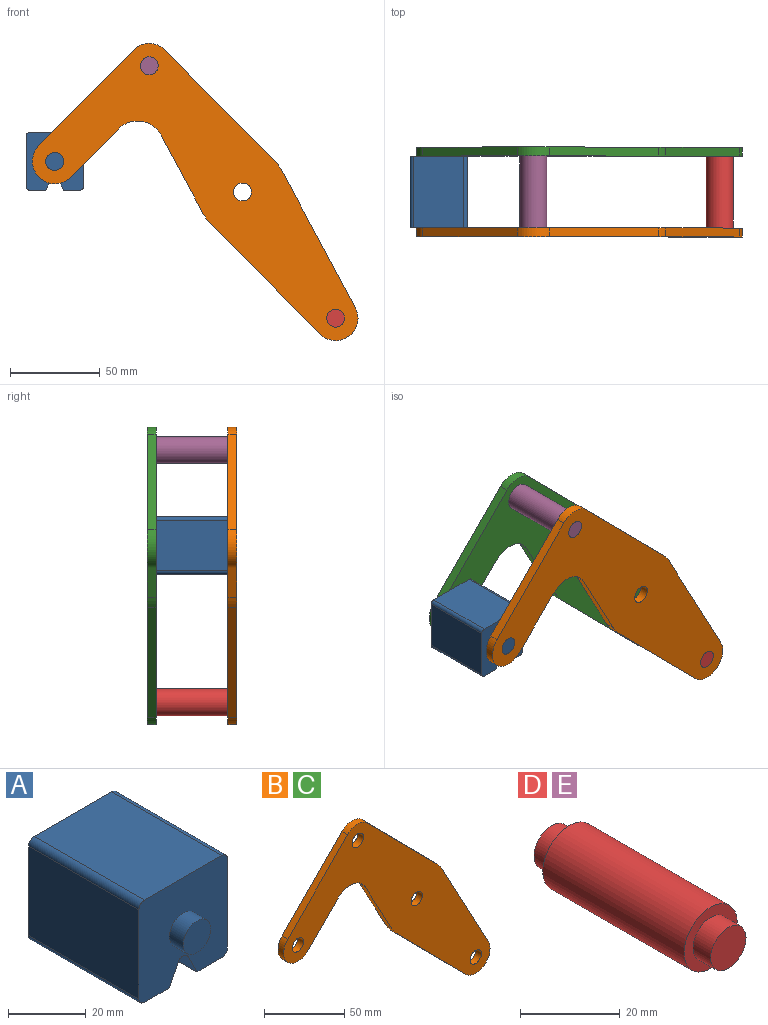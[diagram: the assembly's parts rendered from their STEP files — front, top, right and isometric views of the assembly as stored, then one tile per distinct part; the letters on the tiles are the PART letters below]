
ASSEMBLY  parts=5 mates=3
PART A: 18 faces, bbox 32.1x50x32.1 mm
  f0: plane 40x28.08mm, normal (1,0,0), area 1123.1mm2, adj f4,f10,f13,f14
  f1: plane 40x9.04mm, normal (0,0,-1), area 361.6mm2, adj f2,f4,f10,f14
  f2: plane 40x6.42mm, normal (-0.89,0,-0.45), area 287.2mm2, adj f1,f4,f10,f15
  f3: plane 40x6.42mm, normal (0.89,0,-0.45), area 287.2mm2, adj f4,f5,f10,f15
  f4: plane 32.08x32.08mm, normal (0,-1,0), area 900.6mm2, adj f0,f1,f2,f3,f5,f6,f7,f9
  f5: plane 40x9.04mm, normal (0,0,-1), area 361.6mm2, adj f3,f4,f10,f16
  f6: plane 40x28.08mm, normal (0,0,1), area 1123.1mm2, adj f4,f10,f13,f17
  f7: plane 40x28.08mm, normal (-1,0,0), area 1123.1mm2, adj f4,f10,f16,f17
  f8: plane 10x10mm, normal (0,-1,0), area 78.5mm2, adj f9
  f9: cylinder r=5mm len=10mm, axis (0,1,0), area 157.1mm2, adj f4,f8
  f10: plane 32.08x32.08mm, normal (0,1,0), area 900.6mm2, adj f0,f1,f2,f3,f5,f6,f7,f12
  f11: plane 10x10mm, normal (0,1,0), area 78.5mm2, adj f12
  f12: cylinder r=5mm len=10mm, axis (0,-1,0), area 157.1mm2, adj f10,f11
  f13: cylinder r=2mm len=40mm, axis (0,1,0), area 125.7mm2, adj f0,f4,f6,f10
  f14: cylinder r=2mm len=40mm, axis (0,-1,0), area 125.7mm2, adj f0,f1,f4,f10
  f15: cylinder r=2mm len=40mm, axis (0,1,0), area 177.1mm2, adj f2,f3,f4,f10
  f16: cylinder r=2mm len=40mm, axis (0,1,0), area 125.7mm2, adj f4,f5,f7,f10
  f17: cylinder r=2mm len=40mm, axis (0,-1,0), area 125.7mm2, adj f4,f6,f7,f10
PART B: 18 faces, bbox 181.7x5x165.8 mm
  f0: plane 43.49x23.35mm, normal (-0.88,0,-0.47), area 246.8mm2, adj f1,f14,f16,f17
  f1: cylinder r=25mm len=5.75mm, axis (0,1,0), area 35.8mm2, adj f0,f2,f16,f17
  f2: plane 61.6x60.87mm, normal (-0.71,0,-0.7), area 433mm2, adj f1,f3,f16,f17
  f3: cylinder r=12.5mm len=21.39mm, axis (0,1,0), area 178.4mm2, adj f2,f4,f16,f17
  f4: plane 76.3x40.96mm, normal (0.88,0,0.47), area 433mm2, adj f3,f5,f16,f17
  f5: cylinder r=25mm len=5.75mm, axis (0,1,0), area 35.8mm2, adj f4,f6,f16,f17
  f6: plane 61.6x60.87mm, normal (0.71,0,0.7), area 433mm2, adj f5,f7,f16,f17
  f7: cylinder r=12.5mm len=17.78mm, axis (0,1,0), area 98.9mm2, adj f6,f8,f16,f17
  f8: plane 53.35x52.71mm, normal (-0.71,0,0.7), area 375mm2, adj f7,f9,f16,f17
  f9: cylinder r=12.5mm len=21.39mm, axis (0,1,0), area 196.3mm2, adj f8,f10,f16,f17
  f10: plane 26.86x26.54mm, normal (0.71,0,-0.7), area 188.8mm2, adj f9,f14,f16,f17
  f11: cylinder r=5mm len=10mm, axis (0,1,0), area 157.1mm2, adj f16,f17
  f12: cylinder r=5mm len=10mm, axis (0,1,0), area 157.1mm2, adj f16,f17
  f13: cylinder r=5mm len=10mm, axis (0,1,0), area 157.1mm2, adj f16,f17
  f14: cylinder r=15mm len=23.89mm, axis (0,1,0), area 140.2mm2, adj f0,f10,f16,f17
  f15: cylinder r=5mm len=10mm, axis (0,1,0), area 157.1mm2, adj f16,f17
  f16: plane 181.66x165.78mm, normal (0,-1,0), area 8710.1mm2, adj f0,f1,f2,f3,f4,f5,f6,f7
  f17: plane 181.66x165.78mm, normal (0,1,0), area 8710.1mm2, adj f0,f1,f2,f3,f4,f5,f6,f7
PART C: same geometry as B
PART D: 7 faces, bbox 15x50x15 mm
  f0: cylinder r=7.5mm len=40mm, axis (0,-1,0), area 1885mm2, adj f2,f5
  f1: cylinder r=5mm len=10mm, axis (0,1,0), area 157.1mm2, adj f2,f3
  f2: plane 15x15mm, normal (0,-1,0), area 98.2mm2, adj f0,f1
  f3: plane 10x10mm, normal (0,-1,0), area 78.5mm2, adj f1
  f4: cylinder r=5mm len=10mm, axis (0,-1,0), area 157.1mm2, adj f5,f6
  f5: plane 15x15mm, normal (0,1,0), area 98.2mm2, adj f0,f4
  f6: plane 10x10mm, normal (0,1,0), area 78.5mm2, adj f4
PART E: same geometry as D
PLACE A t=(0,-20,0)mm
PLACE B t=(0,-20,0)mm fixed
PLACE C t=(0,25,0)mm
PLACE D t=(103.95,-20,-140.78)mm
PLACE E t=(0,-20,0)mm
MATE fastened E.f0 <-> C.f7  axis (0,1,0) through (-51.98,20,70.39)mm
MATE revolute A.f9 <-> B.f9  axis (0,-1,0) through (-104.69,-20,17.04)mm
MATE fastened D.f0 <-> B.f3  axis (0,-1,0) through (51.98,-20,-70.39)mm
